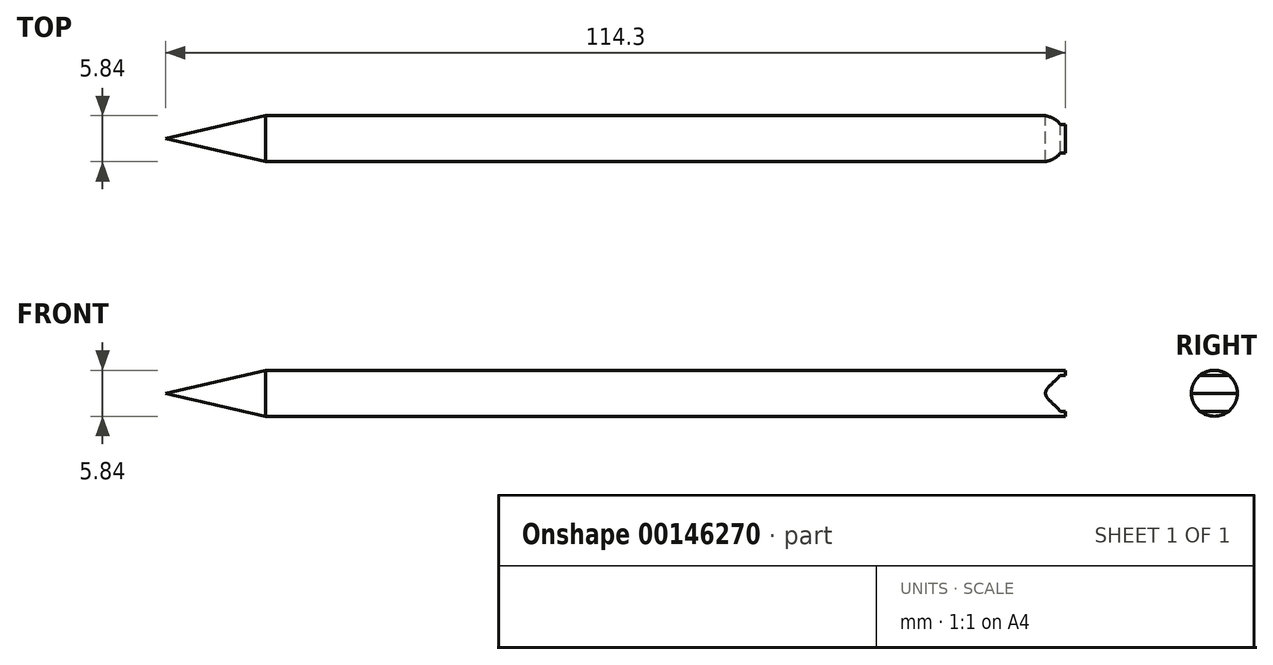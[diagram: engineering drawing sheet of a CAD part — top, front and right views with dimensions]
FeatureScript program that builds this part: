
annotation { "Feature Type Name" : "Feature", "Feature Type Description" : "" }
export const myFeature = defineFeature(function(context is Context, id is Id, definition is map)
    precondition{}
    {
        {
            var Q0;
            Q0=qCreatedBy(makeId("Top.planeOp"),FACE);
            var sketch = newSketch(context, id + "F0", { "sketchPlane" : qUnion([Q0])});
            skLineSegment(sketch, "E0.bottom", {"start": v(-97.14, 28.07) * mm, "end": v(4.46, 28.07) * mm});
            skLineSegment(sketch, "E0.top", {"start": v(-97.14, 22.23) * mm, "end": v(4.46, 22.23) * mm});
            skLineSegment(sketch, "E0.left", {"start": v(-97.14, 28.07) * mm, "end": v(-97.14, 22.23) * mm});
            skLineSegment(sketch, "E0.right", {"start": v(4.46, 28.07) * mm, "end": v(4.46, 22.23) * mm});
            skLineSegment(sketch, "E1.bottom", {"start": v(-109.84, 28.07) * mm, "end": v(-97.14, 28.07) * mm});
            skLineSegment(sketch, "E1.top", {"start": v(-109.84, 22.23) * mm, "end": v(-97.14, 22.23) * mm});
            skLineSegment(sketch, "E1.left", {"start": v(-109.84, 28.07) * mm, "end": v(-109.84, 22.23) * mm});
            skLineSegment(sketch, "E2", {"start": v(-97.14, 28.07) * mm, "end": v(-109.84, 25.15) * mm});
            skLineSegment(sketch, "E3", {"start": v(-109.84, 25.15) * mm, "end": v(-97.14, 22.23) * mm});
            skLineSegment(sketch, "E4", {"start": v(-109.84, 25.15) * mm, "end": v(4.46, 25.15) * mm});
            skSolve(sketch);
        }
        {
            var Q0;
            {var subQ2=sQuery(id+"F0.wireOp",EDGE,"E2");Q0=makeQuery(id+"F0.imprint","IMPRINT",FACE,{"disambiguationData":[TD([[makeQuery(id+"F0.imprint","IMPRINT",EDGE,{"derivedFrom":subQ2}),1.0]])]});}
            var Q1;
            {var subQ0=sQuery(id+"F0.wireOp",EDGE,"E0.bottom");Q1=makeQuery(id+"F0.imprint","IMPRINT",FACE,{"disambiguationData":[TD([[makeQuery(id+"F0.imprint","IMPRINT",EDGE,{"derivedFrom":subQ0}),-1.0]])]});}
            var Q2;
            Q2=sQuery(id+"F0.wireOp",EDGE,"E4");
            revolve(context, id + "F1", {"entities" : qUnion([Q0, Q1]), "axis" : qUnion([Q2]), "revolveType" : RevolveType.FULL});
        }
        {
            var Q0;
            Q0=makeQuery(id+"F1.opRevolve","SWEPT_FACE",FACE,{"disambiguationData":[OSD([sQuery(id+"F0.wireOp",EDGE,"E0.right")])]});
            var sketch = newSketch(context, id + "F2", { "sketchPlane" : qUnion([Q0])});
            skCircle(sketch, "E5.0.0", {"center": v(25.15, 0) * mm, "radius": 2.92 * mm});
            skLineSegment(sketch, "E6.bottom", {"start": v(16.1, 2.29) * mm, "end": v(34.72, 2.29) * mm});
            skLineSegment(sketch, "E6.top", {"start": v(16.1, -2.29) * mm, "end": v(34.72, -2.29) * mm});
            skLineSegment(sketch, "E6.left", {"start": v(16.1, 2.29) * mm, "end": v(16.1, -2.29) * mm});
            skLineSegment(sketch, "E6.right", {"start": v(34.72, 2.29) * mm, "end": v(34.72, -2.29) * mm});
            skSolve(sketch);
        }
        {
            var Q0;
            {var subQ0=sQuery(id+"F2.wireOp",EDGE,"E6.top");var subQ1=sQuery(id+"F2.wireOp",EDGE,"E5.0.0");var subQ2=makeQuery(id+"F2.imprint","INTERSECT",VERTEX,{"disambiguationData":[OD(0.0)],"derivedFrom":[subQ1,subQ0]});Q0=makeQuery(id+"F2.imprint","IMPRINT",FACE,{"disambiguationData":[TD([[makeQuery(id+"F2.imprint","IMPRINT",EDGE,{"disambiguationData":[TD([[subQ2,1.0]])],"derivedFrom":subQ1}),-1.0]])]});}
            extrude(context, id + "F3", {"entities" : qUnion([Q0]), "operationType" : NewBodyOperationType.REMOVE, "oppositeDirection" : true, "depth" : 2.54 * mm});
        }
        {
            var Q0;
            Q0=makeQuery(id+"F3.boolean.opBoolean","COPY",EDGE,{"derivedFrom":makeQuery(id+"F3.opExtrude","CAP_EDGE",EDGE,{"disambiguationData":[OSD([sQuery(id+"F2.wireOp",EDGE,"E6.bottom")])],"isStart":false})});
            var Q1;
            Q1=makeQuery(id+"F3.boolean.opBoolean","COPY",EDGE,{"derivedFrom":makeQuery(id+"F3.opExtrude","CAP_EDGE",EDGE,{"disambiguationData":[OSD([sQuery(id+"F2.wireOp",EDGE,"E6.top")])],"isStart":false})});
            chamfer(context, id + "F4", {"entities" : qUnion([Q0, Q1]), "width" : 1.9 * mm, "tangentPropagation" : true});
        }
        {
            var Q0;
            {var subQ0=sQuery(id+"F2.wireOp",EDGE,"E6.bottom");Q0=makeQuery(id+"F4.opChamfer","BLEND_EDGE",EDGE,{"blendedFrom":[makeQuery(id+"F3.boolean.opBoolean","COPY",EDGE,{"derivedFrom":makeQuery(id+"F3.opExtrude","CAP_EDGE",EDGE,{"disambiguationData":[OSD([subQ0])],"isStart":false})}),makeQuery(id+"F3.boolean.opBoolean","COPY",FACE,{"derivedFrom":makeQuery(id+"F3.opExtrude","CAP_FACE",FACE,{"disambiguationData":[OSD([sQuery(id+"F2.wireOp",EDGE,"E5.0.0"),subQ0,sQuery(id+"F2.wireOp",EDGE,"E6.top")])],"isStart":false})})],"blendedInto":[makeQuery(id+"F3.boolean.opBoolean","COPY",FACE,{"derivedFrom":makeQuery(id+"F3.opExtrude","CAP_FACE",FACE,{"disambiguationData":[OSD([sQuery(id+"F2.wireOp",EDGE,"E5.0.0"),subQ0,sQuery(id+"F2.wireOp",EDGE,"E6.top")])],"isStart":false})})]});}
            var Q1;
            {var subQ0=sQuery(id+"F2.wireOp",EDGE,"E6.top");Q1=makeQuery(id+"F4.opChamfer","BLEND_EDGE",EDGE,{"blendedFrom":[makeQuery(id+"F3.boolean.opBoolean","COPY",EDGE,{"derivedFrom":makeQuery(id+"F3.opExtrude","CAP_EDGE",EDGE,{"disambiguationData":[OSD([subQ0])],"isStart":false})}),makeQuery(id+"F3.boolean.opBoolean","COPY",FACE,{"derivedFrom":makeQuery(id+"F3.opExtrude","CAP_FACE",FACE,{"disambiguationData":[OSD([sQuery(id+"F2.wireOp",EDGE,"E5.0.0"),sQuery(id+"F2.wireOp",EDGE,"E6.bottom"),subQ0])],"isStart":false})})],"blendedInto":[makeQuery(id+"F3.boolean.opBoolean","COPY",FACE,{"derivedFrom":makeQuery(id+"F3.opExtrude","CAP_FACE",FACE,{"disambiguationData":[OSD([sQuery(id+"F2.wireOp",EDGE,"E5.0.0"),sQuery(id+"F2.wireOp",EDGE,"E6.bottom"),subQ0])],"isStart":false})})]});}
            fillet(context, id + "F5", {"entities" : qUnion([Q0, Q1]), "radius" : 1.27 * mm, "tangentPropagation" : true, "allowEdgeOverflow" : false});
        }
    });
